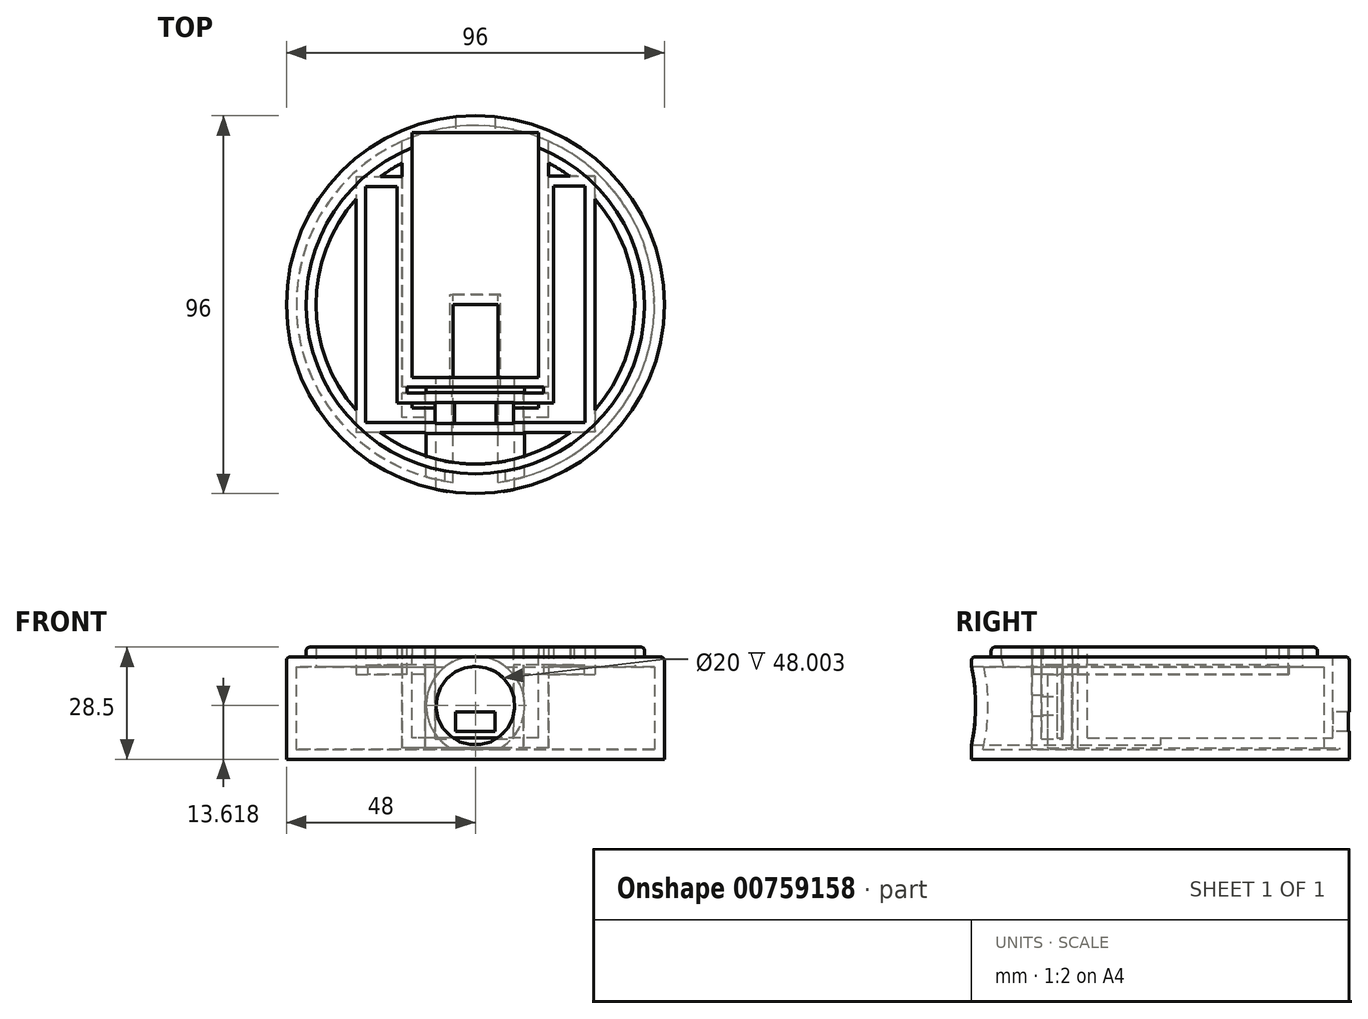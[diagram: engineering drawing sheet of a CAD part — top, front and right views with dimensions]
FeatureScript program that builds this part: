
annotation { "Feature Type Name" : "Feature", "Feature Type Description" : "" }
export const myFeature = defineFeature(function(context is Context, id is Id, definition is map)
    precondition{}
    {
        {
            var Q0;
            Q0=qCreatedBy(makeId("Top.planeOp"),FACE);
            var sketch = newSketch(context, id + "F0", { "sketchPlane" : qUnion([Q0])});
            skCircle(sketch, "E0", {"center": v(0, 0) * mm, "radius": 48 * mm});
            skSolve(sketch);
        }
        {
            var Q0;
            Q0=makeQuery(id+"F0.imprint","IMPRINT",FACE,{"disambiguationData":[TD([[makeQuery(id+"F0.imprint","IMPRINT",EDGE,{"derivedFrom":sQuery(id+"F0.wireOp",EDGE,"E0")}),1.0]])]});
            extrude(context, id + "F1", {"entities" : qUnion([Q0]), "depth" : 26 * mm, "offsetDistance" : 25 * mm});
        }
        {
            var Q0;
            Q0=makeQuery(id+"F1.opExtrude","CAP_FACE",FACE,{"disambiguationData":[OSD([sQuery(id+"F0.wireOp",EDGE,"E0")])],"isStart":false});
            var sketch = newSketch(context, id + "F2", { "sketchPlane" : qUnion([Q0])});
            skCircle(sketch, "E1", {"center": v(0, 0) * mm, "radius": 43 * mm});
            skLineSegment(sketch, "E2.bottom", {"start": v(-27.87, 30.03) * mm, "end": v(-19.87, 30.03) * mm});
            skLineSegment(sketch, "E2.top", {"start": v(-27.87, -29.97) * mm, "end": v(-19.87, -29.97) * mm});
            skLineSegment(sketch, "E2.left", {"start": v(-27.87, 30.03) * mm, "end": v(-27.87, -29.97) * mm});
            skLineSegment(sketch, "E2.right", {"start": v(-19.87, 30.03) * mm, "end": v(-19.87, -29.97) * mm});
            skLineSegment(sketch, "E3.bottom", {"start": v(19.87, 30.1) * mm, "end": v(27.87, 30.1) * mm});
            skLineSegment(sketch, "E3.top", {"start": v(19.87, -29.9) * mm, "end": v(27.87, -29.9) * mm});
            skLineSegment(sketch, "E3.left", {"start": v(19.87, 30.1) * mm, "end": v(19.87, -29.9) * mm});
            skLineSegment(sketch, "E3.right", {"start": v(27.87, 30.1) * mm, "end": v(27.87, -29.9) * mm});
            skLineSegment(sketch, "E4.bottom", {"start": v(25.1, -25) * mm, "end": v(25.1, -30) * mm});
            skLineSegment(sketch, "E4.top", {"start": v(-24.9, -25) * mm, "end": v(-24.9, -30) * mm});
            skLineSegment(sketch, "E4.left", {"start": v(25.1, -25) * mm, "end": v(-24.9, -25) * mm});
            skLineSegment(sketch, "E4.right", {"start": v(25.1, -30) * mm, "end": v(-24.9, -30) * mm});
            skSolve(sketch);
        }
        {
            var Q0;
            Q0=makeQuery(id+"F2.imprint","IMPRINT",FACE,{"disambiguationData":[TD([[makeQuery(id+"F2.imprint","IMPRINT",EDGE,{"derivedFrom":sQuery(id+"F2.wireOp",EDGE,"E1")}),1.0]])]});
            extrude(context, id + "F3", {"entities" : qUnion([Q0]), "operationType" : NewBodyOperationType.ADD, "depth" : 2.5 * mm, "offsetDistance" : 25 * mm});
        }
        {
            var Q0;
            Q0=makeQuery(id+"F2.imprint","IMPRINT",FACE,{"disambiguationData":[TD([[makeQuery(id+"F2.imprint","IMPRINT",EDGE,{"derivedFrom":sQuery(id+"F2.wireOp",EDGE,"E2.bottom")}),-1.0]])]});
            var Q1;
            Q1=makeQuery(id+"F2.imprint","IMPRINT",FACE,{"disambiguationData":[TD([[makeQuery(id+"F2.imprint","IMPRINT",EDGE,{"derivedFrom":sQuery(id+"F2.wireOp",EDGE,"E3.bottom")}),-1.0]])]});
            extrude(context, id + "F4", {"entities" : qUnion([Q0, Q1]), "operationType" : NewBodyOperationType.REMOVE, "oppositeDirection" : true, "depth" : 2 * mm, "offsetDistance" : 25 * mm});
        }
        {
            var Q0;
            {var subQ7=sQuery(id+"F2.wireOp",EDGE,"E2.bottom");Q0=makeQuery(id+"F3.boolean.opBoolean","SPLIT",FACE,{"disambiguationData":[TD([makeQuery(id+"F3.opExtrude","SWEPT_FACE",FACE,{"disambiguationData":[OSD([subQ7])]})])],"derivedFrom":makeQuery(id+"F1.opExtrude","CAP_FACE",FACE,{"disambiguationData":[OSD([sQuery(id+"F0.wireOp",EDGE,"E0")])],"isStart":false})});}
            extrude(context, id + "F5", {"entities" : qUnion([Q0]), "operationType" : NewBodyOperationType.REMOVE, "oppositeDirection" : true, "depth" : 2 * mm, "offsetDistance" : 25 * mm});
        }
        {
            var Q0;
            Q0=makeQuery(id+"F3.opExtrude","CAP_FACE",FACE,{"disambiguationData":[OSD([sQuery(id+"F2.wireOp",EDGE,"E1"),sQuery(id+"F2.wireOp",EDGE,"E2.bottom"),sQuery(id+"F2.wireOp",EDGE,"E2.top"),sQuery(id+"F2.wireOp",EDGE,"E2.left"),sQuery(id+"F2.wireOp",EDGE,"E2.right"),sQuery(id+"F2.wireOp",EDGE,"E3.bottom"),sQuery(id+"F2.wireOp",EDGE,"E3.left"),sQuery(id+"F2.wireOp",EDGE,"E3.right"),sQuery(id+"F2.wireOp",EDGE,"E4.bottom"),sQuery(id+"F2.wireOp",EDGE,"E4.left"),sQuery(id+"F2.wireOp",EDGE,"E4.right")])],"isStart":false});
            var sketch = newSketch(context, id + "F6", { "sketchPlane" : qUnion([Q0])});
            skLineSegment(sketch, "E5.bottom", {"start": v(17.5, -18.5) * mm, "end": v(-17.5, -18.5) * mm});
            skLineSegment(sketch, "E5.top", {"start": v(17.5, -48.5) * mm, "end": v(-17.5, -48.5) * mm});
            skLineSegment(sketch, "E5.left", {"start": v(17.5, -18.5) * mm, "end": v(17.5, -48.5) * mm});
            skLineSegment(sketch, "E5.right", {"start": v(-17.5, -18.5) * mm, "end": v(-17.5, -48.5) * mm});
            skPoint(sketch, "E5.middle", {"position": v(0, -33.5) * mm});
            skLineSegment(sketch, "E6.bottom", {"start": v(16.06, -26.24) * mm, "end": v(-16.06, -26.24) * mm});
            skLineSegment(sketch, "E6.top", {"start": v(16.06, 43.76) * mm, "end": v(-16.06, 43.76) * mm});
            skLineSegment(sketch, "E6.left", {"start": v(16.06, -26.24) * mm, "end": v(16.06, 43.76) * mm});
            skLineSegment(sketch, "E6.right", {"start": v(-16.06, -26.24) * mm, "end": v(-16.06, 43.76) * mm});
            skPoint(sketch, "E6.middle", {"position": v(0, 8.76) * mm});
            skSolve(sketch);
        }
        {
            var Q0;
            Q0=qCreatedBy(makeId("Front.planeOp"),FACE);
            var sketch = newSketch(context, id + "F7", { "sketchPlane" : qUnion([Q0])});
            skCircle(sketch, "E7", {"center": v(0, 13.62) * mm, "radius": 10 * mm});
            skSolve(sketch);
        }
        {
            var Q0;
            Q0 = qSketchRegion(id + "F7", true);
            extrude(context, id + "F8", {"entities" : qUnion([Q0]), "operationType" : NewBodyOperationType.REMOVE, "depth" : 111 * mm, "offsetDistance" : 25 * mm});
        }
        {
            var Q0;
            {var subQ0=sQuery(id+"F6.wireOp",EDGE,"Xm5AUfZa-APQZ-x8uw-voNr-aGvzLEq4ImAc.left");var subQ4=makeQuery(id+"F3.opExtrude","CAP_EDGE",EDGE,{"disambiguationData":[OSD([sQuery(id+"F2.wireOp",EDGE,"E4.right")])],"isStart":false});var subQ5=makeQuery(id+"F6.imprint","INTERSECT",VERTEX,{"derivedFrom":[subQ4,subQ0]});Q0=makeQuery(id+"F6.imprint","IMPRINT",FACE,{"disambiguationData":[TD([[makeQuery(id+"F6.imprint","IMPRINT",EDGE,{"disambiguationData":[TD([[subQ5,1.0]])],"derivedFrom":subQ4}),-1.0]])]});}
            var sketch = newSketch(context, id + "F9", { "sketchPlane" : qUnion([Q0])});
            skLineSegment(sketch, "E8.bottom", {"start": v(-10.29, -24.8) * mm, "end": v(9.71, -24.8) * mm});
            skLineSegment(sketch, "E8.top", {"start": v(-10.29, -30.2) * mm, "end": v(9.71, -30.2) * mm});
            skLineSegment(sketch, "E8.left", {"start": v(-10.29, -24.8) * mm, "end": v(-10.29, -30.2) * mm});
            skLineSegment(sketch, "E8.right", {"start": v(9.71, -24.8) * mm, "end": v(9.71, -30.2) * mm});
            skSolve(sketch);
        }
        {
            var Q0;
            Q0 = qSketchRegion(id + "F9", true);
            extrude(context, id + "F10", {"entities" : qUnion([Q0]), "operationType" : NewBodyOperationType.REMOVE, "oppositeDirection" : true, "depth" : 23.4 * mm, "offsetDistance" : 25 * mm});
        }
        {
            var Q0;
            Q0=makeQuery(id+"F1.opExtrude","CAP_EDGE",EDGE,{"disambiguationData":[OSD([sQuery(id+"F0.wireOp",EDGE,"E0")])],"isStart":false});
            fillet(context, id + "F11", {"entities" : qUnion([Q0]), "radius" : 0.97 * mm, "tangentPropagation" : true, "allowEdgeOverflow" : false});
        }
        {
            var Q0;
            Q0=makeQuery(id+"F3.opExtrude","CAP_EDGE",EDGE,{"disambiguationData":[OSD([sQuery(id+"F2.wireOp",EDGE,"E1")])],"isStart":false});
            fillet(context, id + "F12", {"entities" : qUnion([Q0]), "radius" : 1 * mm, "tangentPropagation" : true, "allowEdgeOverflow" : false});
        }
        {
            var Q0;
            {var subQ0=sQuery(id+"F6.wireOp",EDGE,"E6.bottom");Q0=makeQuery(id+"F6.imprint","IMPRINT",FACE,{"disambiguationData":[TD([[makeQuery(id+"F6.imprint","IMPRINT",EDGE,{"derivedFrom":subQ0}),-1.0]])]});}
            var Q1;
            {var subQ0=sQuery(id+"F6.wireOp",EDGE,"E6.top");Q1=makeQuery(id+"F6.imprint","IMPRINT",FACE,{"disambiguationData":[TD([[makeQuery(id+"F6.imprint","IMPRINT",EDGE,{"derivedFrom":subQ0}),1.0]])]});}
            var Q2;
            {var subQ7=sQuery(id+"F6.wireOp",EDGE,"E5.bottom");Q2=makeQuery(id+"F6.imprint","IMPRINT",FACE,{"disambiguationData":[TD([[makeQuery(id+"F6.imprint","IMPRINT",EDGE,{"derivedFrom":subQ7}),-1.0]])]});}
            extrude(context, id + "F13", {"entities" : qUnion([Q0, Q1, Q2]), "operationType" : NewBodyOperationType.REMOVE, "oppositeDirection" : true, "depth" : 23.1 * mm, "offsetDistance" : 25 * mm});
        }
        {
            var Q0;
            Q0=qCreatedBy(makeId("Front.planeOp"),FACE);
            var sketch = newSketch(context, id + "F14", { "sketchPlane" : qUnion([Q0])});
            skLineSegment(sketch, "E9.bottom", {"start": v(17.53, 0.61) * mm, "end": v(-17.6, 0.61) * mm});
            skLineSegment(sketch, "E9.top", {"start": v(17.53, 24.7) * mm, "end": v(-17.6, 24.7) * mm});
            skLineSegment(sketch, "E9.left", {"start": v(17.53, 0.61) * mm, "end": v(17.53, 24.7) * mm});
            skLineSegment(sketch, "E9.right", {"start": v(-17.6, 0.61) * mm, "end": v(-17.6, 24.7) * mm});
            skPoint(sketch, "E9.middle", {"position": v(-0.04, 12.66) * mm});
            skSolve(sketch);
        }
        {
            var Q0;
            {var subQ0=sQuery(id+"F2.wireOp",EDGE,"E3.bottom");var subQ1=sQuery(id+"F2.wireOp",EDGE,"E3.right");var subQ2=sQuery(id+"F2.wireOp",EDGE,"E2.right");var subQ3=sQuery(id+"F2.wireOp",EDGE,"E2.top");var subQ4=sQuery(id+"F2.wireOp",EDGE,"E4.right");var subQ6=sQuery(id+"F2.wireOp",EDGE,"E3.left");var subQ7=sQuery(id+"F2.wireOp",EDGE,"E2.bottom");var subQ8=sQuery(id+"F2.wireOp",EDGE,"E4.left");var subQ12=sQuery(id+"F2.wireOp",EDGE,"E1");var subQ13=sQuery(id+"F2.wireOp",EDGE,"E2.left");var subQ15=sQuery(id+"F2.wireOp",EDGE,"E4.bottom");var subQ25=makeQuery(id+"F3.opExtrude","CAP_FACE",FACE,{"disambiguationData":[OSD([subQ12,subQ7,subQ3,subQ13,subQ2,subQ0,subQ6,subQ1,subQ15,subQ8,subQ4])],"isStart":false});Q0=makeQuery(id+"F13.boolean.opBoolean","SPLIT",FACE,{"disambiguationData":[TD([makeQuery(id+"F3.opExtrude","SWEPT_FACE",FACE,{"disambiguationData":[OSD([subQ7])]})])],"derivedFrom":subQ25});}
            shell(context, id + "F15", {"entities" : qUnion([Q0]), "thickness" : 2.5 * mm});
        }
        {
            var Q0;
            Q0=makeQuery(id+"F14.imprint","IMPRINT",FACE,{"disambiguationData":[TD([[makeQuery(id+"F14.imprint","IMPRINT",EDGE,{"derivedFrom":sQuery(id+"F14.wireOp",EDGE,"E9.bottom")}),-1.0]])]});
            var sketch = newSketch(context, id + "F16", { "sketchPlane" : qUnion([Q0])});
            skLineSegment(sketch, "E10.bottom", {"start": v(-5, 7.02) * mm, "end": v(5, 7.02) * mm});
            skLineSegment(sketch, "E10.top", {"start": v(-5, 12.02) * mm, "end": v(5, 12.02) * mm});
            skLineSegment(sketch, "E10.left", {"start": v(-5, 7.02) * mm, "end": v(-5, 12.02) * mm});
            skLineSegment(sketch, "E10.right", {"start": v(5, 7.02) * mm, "end": v(5, 12.02) * mm});
            skPoint(sketch, "E10.middle", {"position": v(0, 9.52) * mm});
            skSolve(sketch);
        }
        {
            var Q0;
            Q0 = qSketchRegion(id + "F16", true);
            extrude(context, id + "F17", {"entities" : qUnion([Q0]), "operationType" : NewBodyOperationType.REMOVE, "oppositeDirection" : true, "depth" : 99.2 * mm, "offsetDistance" : 25 * mm});
        }
    });
